# Revit family: Partition-12_Panels_High-Skyfold_Classic_Compact-22-1_to_24-2_FC_6730_to_7365
name_source: partatom
category: Generic Models
units: mm (PartAtom-declared; Revit-internal decimal feet)

## family parameters
Always vertical = Yes
Can host rebar = No
Cut with Voids When Loaded = No
Host = Ceiling
Maintain Annotation Orientation = No
Part Type = Normal
Room Calculation Point = No
Round Connector Dimension = Use Diameter
Shared = No

## types (6) — shared parameters
Default Elevation = 0' - 0"
Description = Custom Powerlift Partitions
Distance From Acoustic Barrier = 0' - 2"
Manufacturer = Skyfold
Model = Compact Drive System
URL = http://www.skyfold.com
Wall Thickness = 0' - 11 3/4"

## per-type parameters (varying)
| type | Acoustic Barrier"C" | Beam Height"B" | Finished Ceiling"A" | Panel Height"F" | Pocket Depth"D" | Pocket Width"E" | Total Panel Height |
| 24'- 0" | 27' - 1 1/2" | 28' - 5" | 24' - 0" | 2' - 2 3/8" | 3' - 1 1/2" | 5' - 3 1/2" | 26' - 10 1/2" |
| 22' -6" | 25' - 7 1/2" | 26' - 11" | 22' - 6" | 2' - 0 7/8" | 3' - 1 1/2" | 5' - 0 1/2" | 25' - 4 1/2" |
| 23' - 0" | 26' - 1 1/2" | 27' - 5" | 23' - 0" | 2' - 1 3/8" | 3' - 1 1/2" | 5' - 1 1/2" | 25' - 10 1/2" |
| 22' - 1" | 25' - 2 1/4" | 26' - 5 3/4" | 22' - 1" | 2' - 0 7/16" | 3' - 1 1/4" | 4' - 11 5/8" | 24' - 11 1/4" |
| 23' - 6" | 26' - 7 1/2" | 27' - 11" | 23' - 6" | 2' - 1 7/8" | 3' - 1 1/2" | 5' - 2 1/2" | 26' - 4 1/2" |
| 24' - 2" | 27' - 3" | 28' - 6 1/2" | 24' - 2" | 2' - 2 1/2" | 3' - 1" | 5' - 3 3/4" | 27' - 0" |

## geometry (parser evidence)
native form markers: Sweep x29
no freeform markers — native parametric forms only
